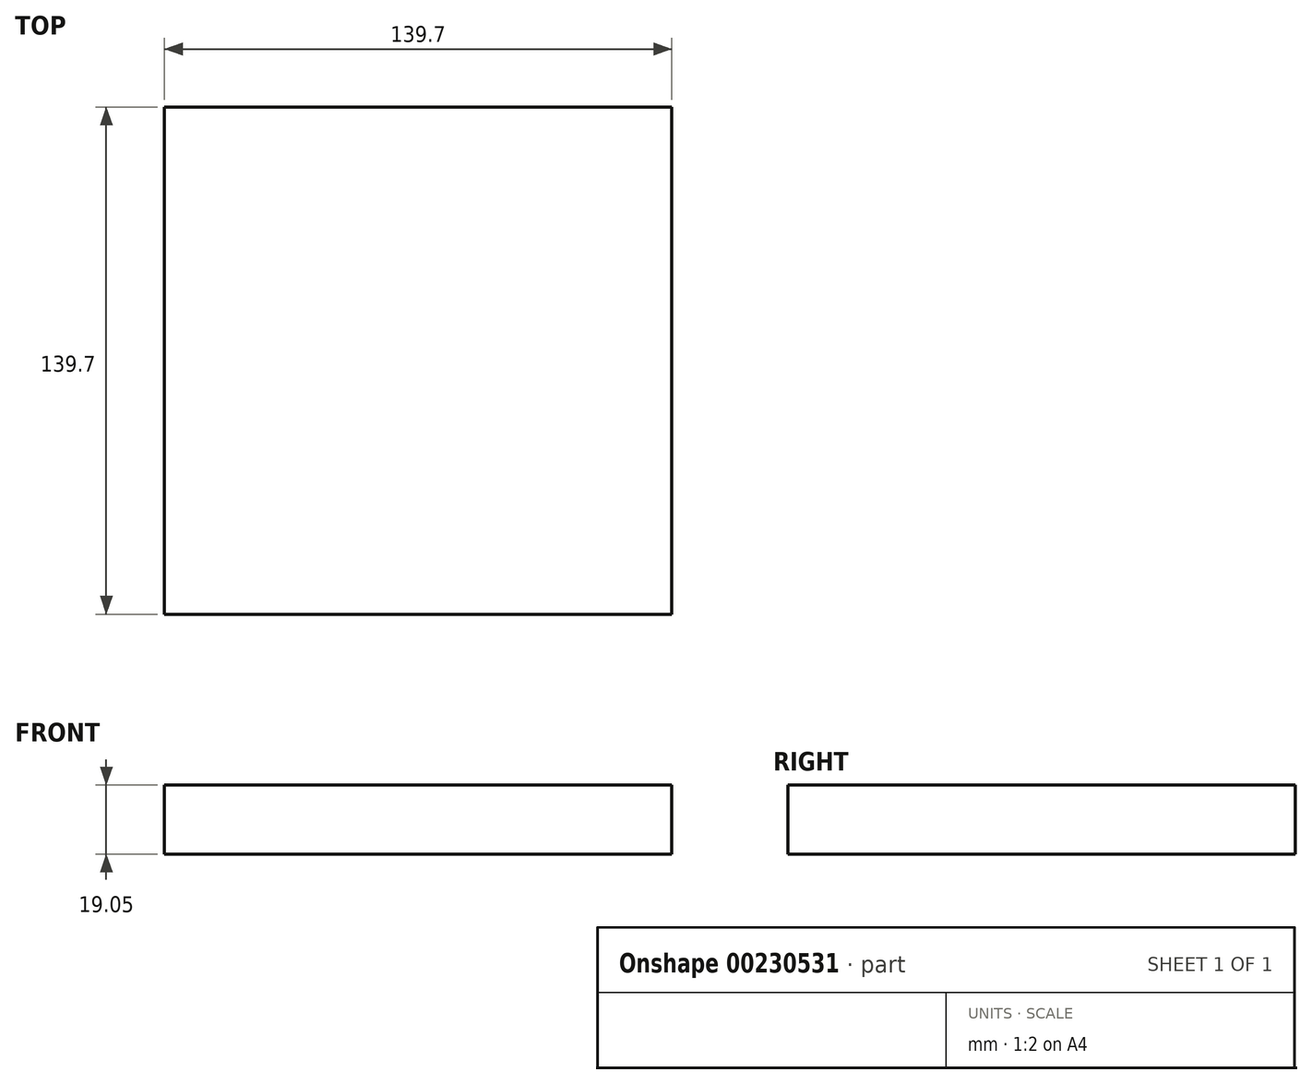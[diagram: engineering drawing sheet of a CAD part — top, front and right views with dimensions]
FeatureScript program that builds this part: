
annotation { "Feature Type Name" : "Feature", "Feature Type Description" : "" }
export const myFeature = defineFeature(function(context is Context, id is Id, definition is map)
    precondition{}
    {
        {
            var Q0;
            Q0=qCreatedBy(makeId("Top.planeOp"),FACE);
            var sketch = newSketch(context, id + "F0", { "sketchPlane" : qUnion([Q0])});
            skLineSegment(sketch, "E0.bottom", {"start": v(-69.85, -69.85) * mm, "end": v(69.85, -69.85) * mm});
            skLineSegment(sketch, "E0.top", {"start": v(-69.85, 69.85) * mm, "end": v(69.85, 69.85) * mm});
            skLineSegment(sketch, "E0.left", {"start": v(-69.85, -69.85) * mm, "end": v(-69.85, 69.85) * mm});
            skLineSegment(sketch, "E0.right", {"start": v(69.85, -69.85) * mm, "end": v(69.85, 69.85) * mm});
            skPoint(sketch, "E0.middle", {"position": v(0, 0) * mm});
            skSolve(sketch);
        }
        {
            var Q0;
            Q0=makeQuery(id+"F0.imprint","IMPRINT",FACE,{"disambiguationData":[TD([[makeQuery(id+"F0.imprint","IMPRINT",EDGE,{"derivedFrom":sQuery(id+"F0.wireOp",EDGE,"E0.bottom")}),1.0]])]});
            extrude(context, id + "F1", {"entities" : qUnion([Q0]), "depth" : 19.05 * mm});
        }
    });
